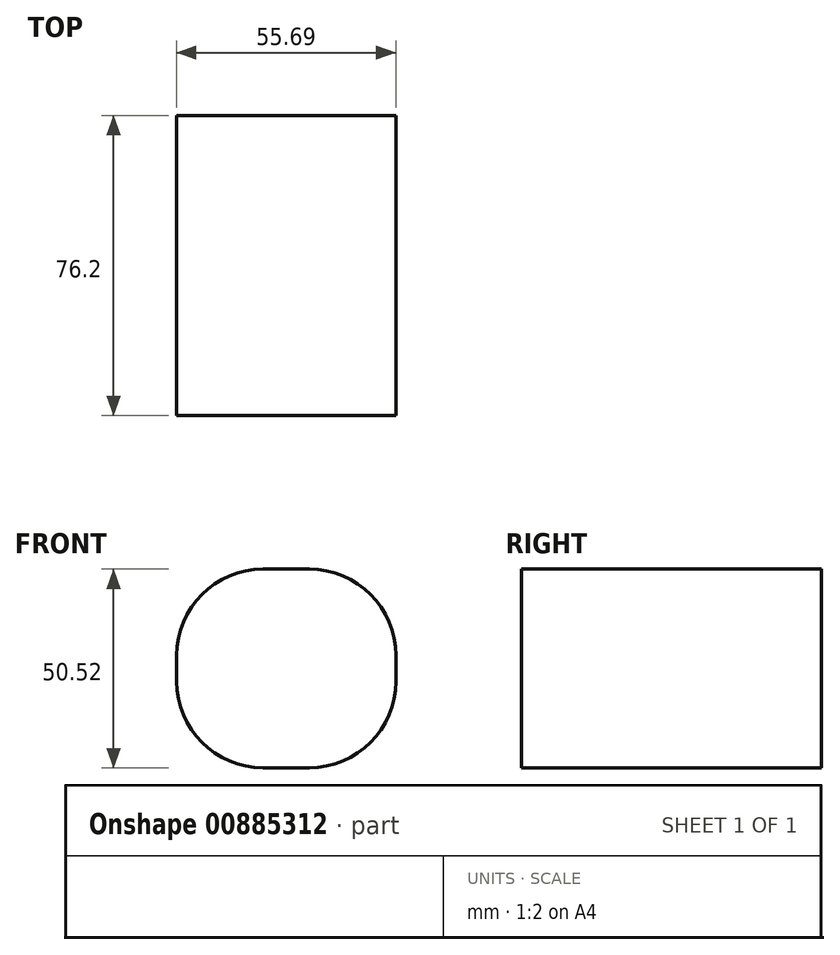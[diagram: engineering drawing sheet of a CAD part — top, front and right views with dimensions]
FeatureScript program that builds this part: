
annotation { "Feature Type Name" : "Feature", "Feature Type Description" : "" }
export const myFeature = defineFeature(function(context is Context, id is Id, definition is map)
    precondition{}
    {
        {
            var Q0;
            Q0=qCreatedBy(makeId("Front.planeOp"),FACE);
            var sketch = newSketch(context, id + "F0", { "sketchPlane" : qUnion([Q0])});
            skLineSegment(sketch, "E0.bottom", {"start": v(-21.97, 0) * mm, "end": v(-33.72, 0) * mm});
            skLineSegment(sketch, "E0.top", {"start": v(-21.97, 50.52) * mm, "end": v(-33.72, 50.52) * mm});
            skLineSegment(sketch, "E0.left", {"start": v(0, 21.97) * mm, "end": v(0, 28.55) * mm});
            skLineSegment(sketch, "E0.right", {"start": v(-55.69, 21.97) * mm, "end": v(-55.69, 28.55) * mm});
            skPoint(sketch, "E0.middle", {"position": v(-27.84, 25.26) * mm});
            skPoint(sketch, "E1.visualSharp", {"position": v(-55.69, 50.52) * mm});
            skArc(sketch, "E1.filletArc", {"start": v(-33.72, 50.52) * mm, "mid": v(-49.25, 44.08) * mm, "end": v(-55.69, 28.55) * mm});
            skPoint(sketch, "E2.visualSharp", {"position": v(0, 0) * mm});
            skArc(sketch, "E2.filletArc", {"start": v(-21.97, 0) * mm, "mid": v(-6.43, 6.43) * mm, "end": v(0, 21.97) * mm});
            skPoint(sketch, "E3.visualSharp", {"position": v(0, 50.52) * mm});
            skArc(sketch, "E3.filletArc", {"start": v(0, 28.55) * mm, "mid": v(-6.43, 44.08) * mm, "end": v(-21.97, 50.52) * mm});
            skPoint(sketch, "E4.visualSharp", {"position": v(-55.69, 0) * mm});
            skArc(sketch, "E4.filletArc", {"start": v(-55.69, 21.97) * mm, "mid": v(-49.25, 6.43) * mm, "end": v(-33.72, 0) * mm});
            skSolve(sketch);
        }
        {
            var Q0;
            Q0=makeQuery(id+"F0.imprint","IMPRINT",FACE,{"disambiguationData":[TD([[makeQuery(id+"F0.imprint","IMPRINT",EDGE,{"derivedFrom":sQuery(id+"F0.wireOp",EDGE,"E0.bottom")}),-1.0]])]});
            extrude(context, id + "F1", {"entities" : qUnion([Q0]), "depth" : 76.2 * mm, "offsetDistance" : 25.4 * mm});
        }
    });
